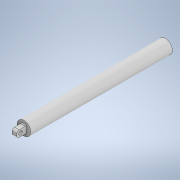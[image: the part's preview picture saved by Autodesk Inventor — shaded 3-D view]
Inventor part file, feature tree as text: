
AUTODESK INVENTOR PART (.ipt)
format: ipt  version: 2021 (Build 250183000, 183)  size: 121,344 bytes
history: native  units: mm
features: extrude x2, fillet x2, sketch x2, hole x1
ambient origin geometry x8: Origin, YZ Plane, XZ Plane, XY Plane, X Axis, Y Axis, Z Axis, Center Point
bodies: Body1 (feature_tree)
feature tree (7):
  extrude  "Extrusion3"  Depth=300.0mm TaperAngle=0.0deg
  extrude  "Extrusion4"  Depth=2.0mm
  fillet  "Fillet1"  Radius=20.0mm
  fillet  "Fillet2"  Radius=10.0mm
  hole  "Hole1"  [1 undecoded]
  sketch  "Sketch3"  dims[d6=29.0mm d7=300.0mm d8=0.0mm]
  sketch  "Sketch4"  dims[d9=7.0mm d10=7.0mm d11=20.0mm d12=10.0mm d13=0.0mm d14=2.0mm d15=5.0mm d16=8.0mm d17=8.0mm d18=6.0mm d19=4.0mm d20=2.0mm d21=90.0deg d22=8.0mm d23=20.594885mm d4=0.5mm d5=0.872665mm]
note: 1 required parameter value undecoded (feature->parameter linkage not recoverable at this tier; creation-order binding heuristic only, values carry confidence <= 0.55)
